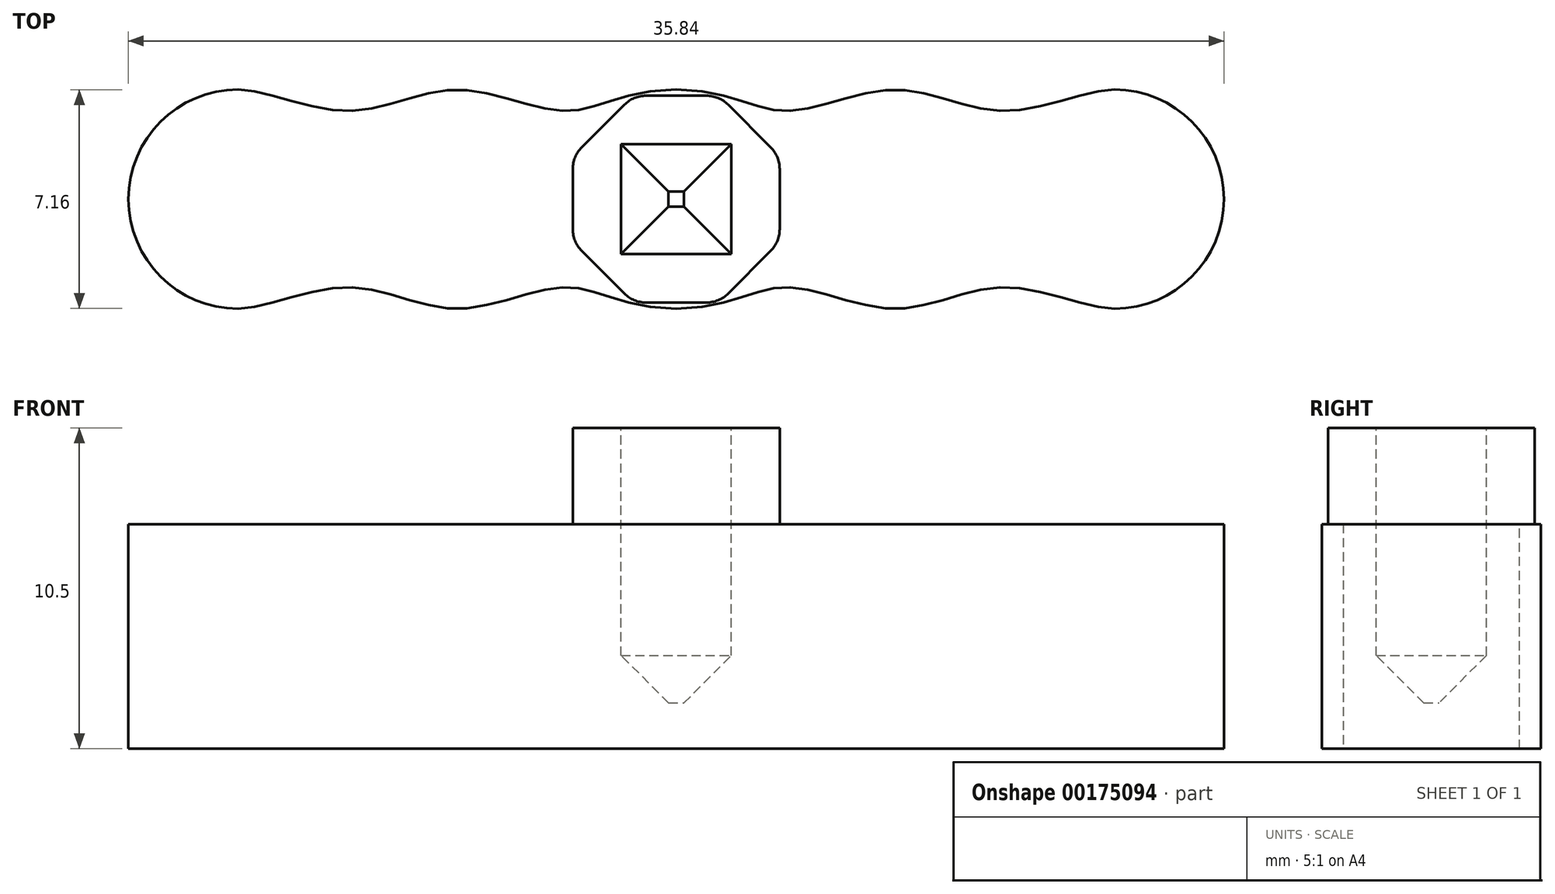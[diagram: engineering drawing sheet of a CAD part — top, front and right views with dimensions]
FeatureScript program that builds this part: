
annotation { "Feature Type Name" : "Feature", "Feature Type Description" : "" }
export const myFeature = defineFeature(function(context is Context, id is Id, definition is map)
    precondition{}
    {
        {
            assignVariable(context, id + "F0", {"name" : "r", "anyValue" : 3.3});
        }
        {
            assignVariable(context, id + "F1", {"name" : "d", "anyValue" : 9});
        }
        {
            var Q0;
            Q0=qCreatedBy(makeId("Top.planeOp"),FACE);
            var sketch = newSketch(context, id + "F2", { "sketchPlane" : qUnion([Q0])});
            skLineSegment(sketch, "E0", {"start": v(0, 0) * mm, "end": v(0, -3.58) * mm, "construction": true});
            skLineSegment(sketch, "E1", {"start": v(0, -2.88) * mm, "end": v(19.49, -2.88) * mm, "construction": true});
            skLineSegment(sketch, "E2", {"start": v(0, -3.58) * mm, "end": v(19.58, -3.58) * mm, "construction": true});
            skLineSegment(sketch, "E3.1.0.0", {"start": v(3.58, 0) * mm, "end": v(3.58, -3.58) * mm, "construction": true});
            skLineSegment(sketch, "E3.2.0.0", {"start": v(7.17, 0) * mm, "end": v(7.17, -3.58) * mm, "construction": true});
            skLineSegment(sketch, "E3.direction1", {"start": v(0, -3.58) * mm, "end": v(3.58, -3.58) * mm, "construction": true});
            skLineSegment(sketch, "E4.0.3.0", {"start": v(10.75, 0) * mm, "end": v(10.75, -3.58) * mm, "construction": true});
            skLineSegment(sketch, "E4.0.4.0", {"start": v(14.33, 0) * mm, "end": v(14.33, -3.58) * mm, "construction": true});
            skArc(sketch, "E5", {"start": v(14.33, -3.58) * mm, "mid": v(16.87, -2.53) * mm, "end": v(17.92, 0) * mm});
            skFitSpline(sketch, "E6", {"points": [v(0, -3.58) * mm, v(3.58, -2.88) * mm, v(7.17, -3.58) * mm, v(10.75, -2.88) * mm, v(14.33, -3.58) * mm], "startDerivative": vector(21.5, 0) * mm, "endDerivative": vector(11.48, 0) * mm});
            skLineSegment(sketch, "E7", {"start": v(-23.13, 0) * mm, "end": v(23.72, 0) * mm, "construction": true});
            skLineSegment(sketch, "E8", {"start": v(0, 13.7) * mm, "end": v(0, -14.93) * mm, "construction": true});
            skLineSegment(sketch, "E9.MirrorCS", {"start": v(10.75, 0) * mm, "end": v(10.75, 3.58) * mm, "construction": true});
            skLineSegment(sketch, "E10.MirrorCS", {"start": v(0, 3.58) * mm, "end": v(19.58, 3.58) * mm, "construction": true});
            skLineSegment(sketch, "E11.MirrorCS", {"start": v(0, 2.88) * mm, "end": v(19.49, 2.88) * mm, "construction": true});
            skLineSegment(sketch, "E12.MirrorCS", {"start": v(14.33, 0) * mm, "end": v(14.33, 3.58) * mm, "construction": true});
            skLineSegment(sketch, "E13.MirrorCS", {"start": v(0, 3.58) * mm, "end": v(3.58, 3.58) * mm, "construction": true});
            skArc(sketch, "E14.MirrorCS", {"start": v(14.33, 3.58) * mm, "mid": v(16.87, 2.53) * mm, "end": v(17.92, 0) * mm});
            skFitSpline(sketch, "E15.MirrorCS", {"points": [v(0, 3.58) * mm, v(3.58, 2.88) * mm, v(7.17, 3.58) * mm, v(10.75, 2.88) * mm, v(14.33, 3.58) * mm], "startDerivative": vector(21.5, 0) * mm, "endDerivative": vector(11.48, 0) * mm});
            skLineSegment(sketch, "E16.MirrorCS", {"start": v(3.58, 0) * mm, "end": v(3.58, 3.58) * mm, "construction": true});
            skLineSegment(sketch, "E17.MirrorCS", {"start": v(7.17, 0) * mm, "end": v(7.17, 3.58) * mm, "construction": true});
            skFitSpline(sketch, "E18.MirrorCS", {"points": [v(0, 3.58) * mm, v(-3.58, 2.88) * mm, v(-7.17, 3.58) * mm, v(-10.75, 2.88) * mm, v(-14.33, 3.58) * mm], "startDerivative": vector(-21.5, 0) * mm, "endDerivative": vector(-11.48, 0) * mm});
            skLineSegment(sketch, "E19.MirrorCS", {"start": v(0, 3.58) * mm, "end": v(-3.58, 3.58) * mm, "construction": true});
            skLineSegment(sketch, "E20.MirrorCS", {"start": v(-14.33, 0) * mm, "end": v(-14.33, 3.58) * mm, "construction": true});
            skLineSegment(sketch, "E21.MirrorCS", {"start": v(23.13, 0) * mm, "end": v(-23.72, 0) * mm, "construction": true});
            skLineSegment(sketch, "E22.MirrorCS", {"start": v(0, 3.58) * mm, "end": v(-19.58, 3.58) * mm, "construction": true});
            skLineSegment(sketch, "E23.MirrorCS", {"start": v(0, -3.58) * mm, "end": v(-3.58, -3.58) * mm, "construction": true});
            skLineSegment(sketch, "E24.MirrorCS", {"start": v(-14.33, 0) * mm, "end": v(-14.33, -3.58) * mm, "construction": true});
            skArc(sketch, "E25.MirrorCS", {"start": v(-14.33, 3.58) * mm, "mid": v(-16.87, 2.53) * mm, "end": v(-17.92, 0) * mm});
            skLineSegment(sketch, "E26.MirrorCS", {"start": v(0, -2.88) * mm, "end": v(-19.49, -2.88) * mm, "construction": true});
            skLineSegment(sketch, "E27.MirrorCS", {"start": v(0, -3.58) * mm, "end": v(-19.58, -3.58) * mm, "construction": true});
            skLineSegment(sketch, "E28.MirrorCS", {"start": v(-10.75, 0) * mm, "end": v(-10.75, -3.58) * mm, "construction": true});
            skArc(sketch, "E29.MirrorCS", {"start": v(-14.33, -3.58) * mm, "mid": v(-16.87, -2.53) * mm, "end": v(-17.92, 0) * mm});
            skLineSegment(sketch, "E30.MirrorCS", {"start": v(-3.58, 0) * mm, "end": v(-3.58, -3.58) * mm, "construction": true});
            skFitSpline(sketch, "E31.MirrorCS", {"points": [v(0, -3.58) * mm, v(-3.58, -2.88) * mm, v(-7.17, -3.58) * mm, v(-10.75, -2.88) * mm, v(-14.33, -3.58) * mm], "startDerivative": vector(-21.5, 0) * mm, "endDerivative": vector(-11.48, 0) * mm});
            skLineSegment(sketch, "E32.MirrorCS", {"start": v(-10.75, 0) * mm, "end": v(-10.75, 3.58) * mm, "construction": true});
            skLineSegment(sketch, "E33.MirrorCS", {"start": v(0, 2.88) * mm, "end": v(-19.49, 2.88) * mm, "construction": true});
            skLineSegment(sketch, "E34.MirrorCS", {"start": v(-3.58, 0) * mm, "end": v(-3.58, 3.58) * mm, "construction": true});
            skLineSegment(sketch, "E35.MirrorCS", {"start": v(-7.17, 0) * mm, "end": v(-7.17, 3.58) * mm, "construction": true});
            skLineSegment(sketch, "E36.MirrorCS", {"start": v(-7.17, 0) * mm, "end": v(-7.17, -3.58) * mm, "construction": true});
            skSolve(sketch);
        }
        {
            var Q0;
            Q0=qSketchRegion(id+"F2",true);
            extrude(context, id + "F3", {"entities" : qUnion([Q0]), "depth" : ((getVariable(context, 'd') + 1.5) * 0.7) * mm});
        }
        {
            var Q0;
            Q0=makeQuery(id+"F3.opExtrude","CAP_FACE",FACE,{"disambiguationData":[OSD([sQuery(id+"F2.wireOp",EDGE,"E5"),sQuery(id+"F2.wireOp",EDGE,"E6"),sQuery(id+"F2.wireOp",EDGE,"E14.MirrorCS"),sQuery(id+"F2.wireOp",EDGE,"E15.MirrorCS"),sQuery(id+"F2.wireOp",EDGE,"E18.MirrorCS"),sQuery(id+"F2.wireOp",EDGE,"E25.MirrorCS"),sQuery(id+"F2.wireOp",EDGE,"E29.MirrorCS"),sQuery(id+"F2.wireOp",EDGE,"E31.MirrorCS")])],"isStart":false});
            var sketch = newSketch(context, id + "F4", { "sketchPlane" : qUnion([Q0])});
            skCircle(sketch, "E37.cCircle", {"center": v(0, 0) * mm, "radius": 3.38 * mm, "construction": true});
            skLineSegment(sketch, "E37.0", {"start": v(0.99, -3.38) * mm, "end": v(-0.99, -3.38) * mm});
            skLineSegment(sketch, "E37.1", {"start": v(-1.7, -3.1) * mm, "end": v(-3.1, -1.7) * mm});
            skLineSegment(sketch, "E37.2", {"start": v(-3.38, -0.99) * mm, "end": v(-3.38, 0.99) * mm});
            skLineSegment(sketch, "E37.3", {"start": v(-3.1, 1.7) * mm, "end": v(-1.7, 3.1) * mm});
            skLineSegment(sketch, "E37.4", {"start": v(-0.99, 3.38) * mm, "end": v(0.99, 3.38) * mm});
            skLineSegment(sketch, "E37.5", {"start": v(1.7, 3.1) * mm, "end": v(3.1, 1.7) * mm});
            skLineSegment(sketch, "E37.6", {"start": v(3.38, 0.99) * mm, "end": v(3.38, -0.99) * mm});
            skLineSegment(sketch, "E37.7", {"start": v(3.1, -1.7) * mm, "end": v(1.7, -3.1) * mm});
            skPoint(sketch, "E37.0.midPoint", {"position": v(0, -3.38) * mm});
            skPoint(sketch, "E38.visualSharp", {"position": v(1.4, -3.38) * mm});
            skArc(sketch, "E38.filletArc", {"start": v(0.99, -3.38) * mm, "mid": v(1.37, -3.3) * mm, "end": v(1.7, -3.1) * mm});
            skPoint(sketch, "E39.visualSharp", {"position": v(-1.4, -3.38) * mm});
            skArc(sketch, "E39.filletArc", {"start": v(-1.7, -3.1) * mm, "mid": v(-1.37, -3.3) * mm, "end": v(-0.99, -3.38) * mm});
            skPoint(sketch, "E40.visualSharp", {"position": v(1.4, 3.38) * mm});
            skArc(sketch, "E40.filletArc", {"start": v(1.7, 3.1) * mm, "mid": v(1.37, 3.3) * mm, "end": v(0.99, 3.38) * mm});
            skPoint(sketch, "E41.visualSharp", {"position": v(-1.4, 3.38) * mm});
            skArc(sketch, "E41.filletArc", {"start": v(-0.99, 3.38) * mm, "mid": v(-1.37, 3.3) * mm, "end": v(-1.7, 3.1) * mm});
            skPoint(sketch, "E42.visualSharp", {"position": v(-3.38, 1.4) * mm});
            skArc(sketch, "E42.filletArc", {"start": v(-3.1, 1.7) * mm, "mid": v(-3.3, 1.37) * mm, "end": v(-3.38, 0.99) * mm});
            skPoint(sketch, "E43.visualSharp", {"position": v(-3.38, -1.4) * mm});
            skArc(sketch, "E43.filletArc", {"start": v(-3.38, -0.99) * mm, "mid": v(-3.3, -1.37) * mm, "end": v(-3.1, -1.7) * mm});
            skPoint(sketch, "E44.visualSharp", {"position": v(3.38, -1.4) * mm});
            skArc(sketch, "E44.filletArc", {"start": v(3.1, -1.7) * mm, "mid": v(3.3, -1.37) * mm, "end": v(3.38, -0.99) * mm});
            skPoint(sketch, "E45.visualSharp", {"position": v(3.38, 1.4) * mm});
            skArc(sketch, "E45.filletArc", {"start": v(3.38, 0.99) * mm, "mid": v(3.3, 1.37) * mm, "end": v(3.1, 1.7) * mm});
            skSolve(sketch);
        }
        {
            var Q0;
            Q0=qSketchRegion(id+"F4",true);
            extrude(context, id + "F5", {"entities" : qUnion([Q0]), "operationType" : NewBodyOperationType.ADD, "depth" : ((getVariable(context, 'd') + 1.5) * 0.3) * mm});
        }
        {
            var Q0;
            Q0=makeQuery(id+"F5.opExtrude","CAP_FACE",FACE,{"disambiguationData":[OSD([sQuery(id+"F4.wireOp",EDGE,"E37.0"),sQuery(id+"F4.wireOp",EDGE,"E37.1"),sQuery(id+"F4.wireOp",EDGE,"E37.2"),sQuery(id+"F4.wireOp",EDGE,"E37.3"),sQuery(id+"F4.wireOp",EDGE,"E37.4"),sQuery(id+"F4.wireOp",EDGE,"E37.5"),sQuery(id+"F4.wireOp",EDGE,"E37.6"),sQuery(id+"F4.wireOp",EDGE,"E37.7"),sQuery(id+"F4.wireOp",EDGE,"E38.filletArc"),sQuery(id+"F4.wireOp",EDGE,"E39.filletArc"),sQuery(id+"F4.wireOp",EDGE,"E40.filletArc"),sQuery(id+"F4.wireOp",EDGE,"E41.filletArc"),sQuery(id+"F4.wireOp",EDGE,"E42.filletArc"),sQuery(id+"F4.wireOp",EDGE,"E43.filletArc"),sQuery(id+"F4.wireOp",EDGE,"E44.filletArc"),sQuery(id+"F4.wireOp",EDGE,"E45.filletArc")])],"isStart":false});
            var sketch = newSketch(context, id + "F6", { "sketchPlane" : qUnion([Q0])});
            skLineSegment(sketch, "E46.bottom", {"start": v(-1.8, 1.8) * mm, "end": v(1.8, 1.8) * mm});
            skLineSegment(sketch, "E46.top", {"start": v(-1.8, -1.8) * mm, "end": v(1.8, -1.8) * mm});
            skLineSegment(sketch, "E46.left", {"start": v(-1.8, 1.8) * mm, "end": v(-1.8, -1.8) * mm});
            skLineSegment(sketch, "E46.right", {"start": v(1.8, 1.8) * mm, "end": v(1.8, -1.8) * mm});
            skLineSegment(sketch, "E47", {"start": v(1.8, 1.8) * mm, "end": v(-1.8, -1.8) * mm, "construction": true});
            skSolve(sketch);
        }
        {
            var Q0;
            Q0=qSketchRegion(id+"F6",true);
            extrude(context, id + "F7", {"entities" : qUnion([Q0]), "operationType" : NewBodyOperationType.REMOVE, "oppositeDirection" : true, "depth" : (getVariable(context, 'd')) * mm});
        }
        {
            var Q0;
            Q0=makeQuery(id+"F7.boolean.opBoolean","COPY",EDGE,{"derivedFrom":makeQuery(id+"F7.opExtrude","CAP_EDGE",EDGE,{"disambiguationData":[OSD([sQuery(id+"F6.wireOp",EDGE,"E46.top")])],"isStart":false})});
            var Q1;
            Q1=makeQuery(id+"F7.boolean.opBoolean","COPY",EDGE,{"derivedFrom":makeQuery(id+"F7.opExtrude","CAP_EDGE",EDGE,{"disambiguationData":[OSD([sQuery(id+"F6.wireOp",EDGE,"E46.right")])],"isStart":false})});
            var Q2;
            Q2=makeQuery(id+"F7.boolean.opBoolean","COPY",EDGE,{"derivedFrom":makeQuery(id+"F7.opExtrude","CAP_EDGE",EDGE,{"disambiguationData":[OSD([sQuery(id+"F6.wireOp",EDGE,"E46.bottom")])],"isStart":false})});
            var Q3;
            Q3=makeQuery(id+"F7.boolean.opBoolean","COPY",EDGE,{"derivedFrom":makeQuery(id+"F7.opExtrude","CAP_EDGE",EDGE,{"disambiguationData":[OSD([sQuery(id+"F6.wireOp",EDGE,"E46.left")])],"isStart":false})});
            chamfer(context, id + "F8", {"entities" : qUnion([Q0, Q1, Q2, Q3]), "width" : (getVariable(context, 'r') / 2 - 0.1) * mm, "tangentPropagation" : true});
        }
    });
